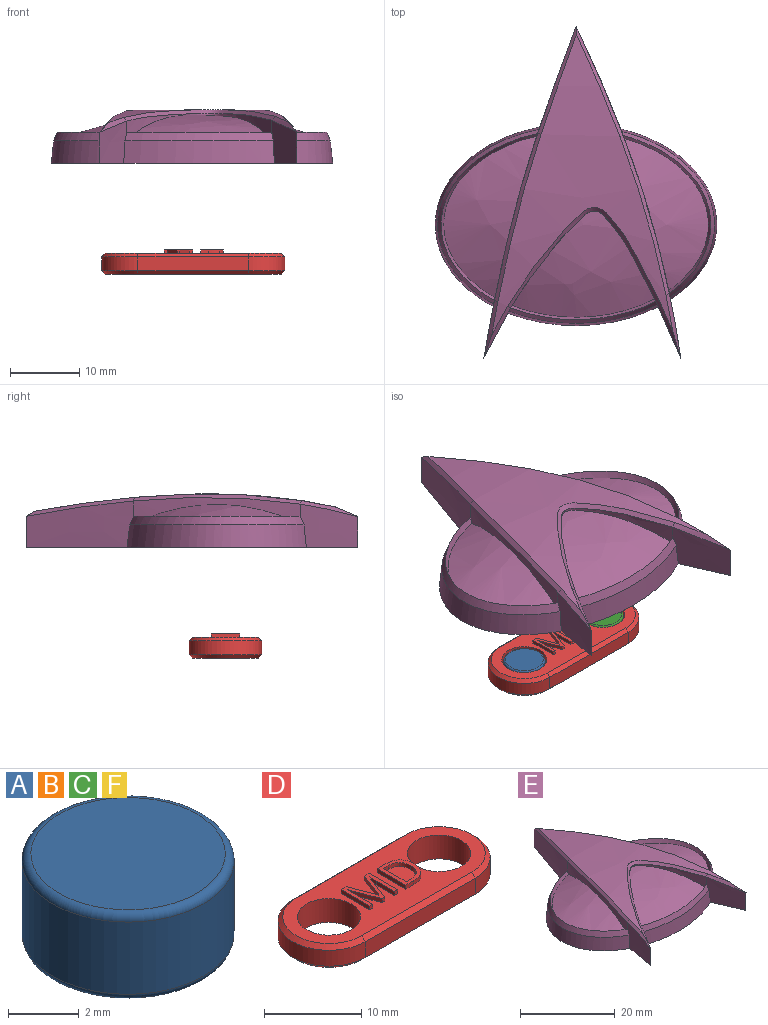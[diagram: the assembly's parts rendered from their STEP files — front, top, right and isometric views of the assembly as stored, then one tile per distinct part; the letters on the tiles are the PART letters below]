
ASSEMBLY  parts=6 mates=5
PART A: 5 faces, bbox 6.5x6.5x3 mm
  f0: cylinder r=3mm len=6mm, axis (0,0,-1), area 47.1mm2, adj f3,f4
  f1: plane 5.5x5.5mm, normal (0,0,1), area 23.8mm2, adj f4
  f2: plane 5.5x5.5mm, normal (0,0,-1), area 23.8mm2, adj f3
  f3: torus R=2.75mm, axis (0,0,1), area 7.2mm2, adj f0,f2
  f4: torus R=2.75mm, axis (0,0,1), area 7.2mm2, adj f0,f1
PART B: same geometry as A
PART C: same geometry as A
PART D: 51 faces, bbox 26.5x10.5x3.5 mm
  f0: plane 25.5x9.5mm, normal (0,0,1), area 137mm2, adj f4,f6,f8,f9,f10,f11,f16,f17
  f1: cylinder r=5.25mm len=10.5mm, axis (0,0,-1), area 33mm2, adj f2,f5,f9,f13
  f2: plane 16x2mm, normal (0,1,0), area 32mm2, adj f1,f3,f11,f15
  f3: cylinder r=5.25mm len=10.5mm, axis (0,0,-1), area 33mm2, adj f2,f5,f10,f14
  f4: cylinder r=3.25mm len=6.5mm, axis (0,0,-1), area 61.3mm2, adj f0,f7
  f5: plane 16x2mm, normal (0,-1,0), area 32mm2, adj f1,f3,f8,f12
  f6: cylinder r=3.25mm len=6.5mm, axis (0,0,-1), area 61.3mm2, adj f0,f7
  f7: plane 25.5x9.5mm, normal (0,0,-1), area 156.5mm2, adj f4,f6,f12,f13,f14,f15
  f8: plane 16x0.5mm, normal (0,-0.71,0.71), area 11.3mm2, adj f0,f5,f9,f10
  f9: cone r=5.25mm half-angle=45deg, axis (0,0,-1), area 11.1mm2, adj f0,f1,f8,f11
  f10: cone r=5.25mm half-angle=45deg, axis (0,0,-1), area 11.1mm2, adj f0,f3,f8,f11
  f11: plane 16x0.5mm, normal (0,0.71,0.71), area 11.3mm2, adj f0,f2,f9,f10
  f12: plane 16x0.5mm, normal (0,-0.71,-0.71), area 11.3mm2, adj f5,f7,f13,f14
  f13: cone r=4.75mm half-angle=45deg, axis (0,0,1), area 11.1mm2, adj f1,f7,f12,f15
  f14: cone r=4.75mm half-angle=45deg, axis (0,0,1), area 11.1mm2, adj f3,f7,f12,f15
  f15: plane 16x0.5mm, normal (0,0.71,-0.71), area 11.3mm2, adj f2,f7,f13,f14
  f16: plane 3.68x1.41mm, normal (-0.93,-0.36,0), area 2mm2, adj f0,f17,f33,f34
  f17: plane 0.5x0.39mm, normal (0,-1,0), area 0.2mm2, adj f0,f16,f18,f34
  f18: plane 3.67x1.42mm, normal (0.93,-0.36,0), area 2mm2, adj f0,f17,f19,f34
  f19: plane 0.5x0.02mm, normal (0,-1,0), area 0mm2, adj f0,f18,f20,f34
  f20: extruded ~1x0.5mm, area 0.5mm2, adj f0,f19,f21,f34
  f21: plane 2.67x0.5mm, normal (-1,0,0), area 1.3mm2, adj f0,f20,f22,f34
  f22: plane 0.5x0.48mm, normal (0,-1,0), area 0.2mm2, adj f0,f21,f23,f34
  f23: plane 4.15x0.5mm, normal (1,0,0), area 2.1mm2, adj f0,f22,f24,f34
  f24: plane 0.72x0.5mm, normal (0,1,0), area 0.4mm2, adj f0,f23,f25,f34
  f25: plane 3.42x1.32mm, normal (-0.93,0.36,0), area 1.8mm2, adj f0,f24,f26,f34
  f26: plane 0.5x0.02mm, normal (0,1,0), area 0mm2, adj f0,f25,f27,f34
  f27: plane 3.42x1.31mm, normal (0.93,0.36,0), area 1.8mm2, adj f0,f26,f28,f34
  f28: plane 0.73x0.5mm, normal (0,1,0), area 0.4mm2, adj f0,f27,f29,f34
  f29: plane 4.15x0.5mm, normal (-1,0,0), area 2.1mm2, adj f0,f28,f30,f34
  f30: plane 0.5x0.45mm, normal (0,-1,0), area 0.2mm2, adj f0,f29,f31,f34
  f31: plane 2.64x0.5mm, normal (1,0,0), area 1.3mm2, adj f0,f30,f32,f34
  f32: extruded ~1.04x0.5mm, area 0.5mm2, adj f0,f31,f33,f34
  f33: plane 0.5x0.02mm, normal (0,-1,0), area 0mm2, adj f0,f16,f32,f34
  f34: plane 4.15x4.11mm, normal (0,0,1), area 7.4mm2, adj f16,f17,f18,f19,f20,f21,f22,f23
  f35: extruded ~1.22x0.5mm, area 0.7mm2, adj f36,f48,f49,f50
  f36: extruded ~1.25x0.5mm, area 0.7mm2, adj f35,f37,f49,f50
  f37: extruded ~1.3x0.5mm, area 0.7mm2, adj f36,f38,f49,f50
  f38: plane 0.59x0.5mm, normal (0,1,0), area 0.3mm2, adj f37,f39,f49,f50
  f39: plane 3.31x0.5mm, normal (1,0,0), area 1.7mm2, adj f38,f40,f49,f50
  f40: plane 0.7x0.5mm, normal (0,-1,0), area 0.4mm2, adj f39,f48,f49,f50
  f41: extruded ~1.57x0.56mm, area 0.9mm2, adj f0,f42,f47,f49
  f42: extruded ~1.5x0.54mm, area 0.8mm2, adj f0,f41,f43,f49
  f43: extruded ~1.5x0.54mm, area 0.8mm2, adj f0,f42,f44,f49
  f44: plane 1.27x0.5mm, normal (0,1,0), area 0.6mm2, adj f0,f43,f45,f49
  f45: plane 4.15x0.5mm, normal (-1,0,0), area 2.1mm2, adj f0,f44,f46,f49
  f46: plane 1.15x0.5mm, normal (0,-1,0), area 0.6mm2, adj f0,f45,f47,f49
  f47: extruded ~1.6x0.54mm, area 0.9mm2, adj f0,f41,f46,f49
  f48: extruded ~1.21x0.5mm, area 0.7mm2, adj f35,f40,f49,f50
  f49: plane 4.15x3.31mm, normal (0,0,1), area 5.4mm2, adj f35,f36,f37,f38,f39,f40,f41,f42
  f50: plane 3.31x2.32mm, normal (0,0,1), area 6.7mm2, adj f35,f36,f37,f38,f39,f40,f48
PART E: 38 faces, bbox 40.7x49.4x10.5 mm
  f0: extruded ~15.84x6.82mm, area 96.5mm2, adj f1,f6,f11,f14,f19,f35
  f1: extruded ~15.54x6.73mm, area 92.1mm2, adj f0,f7,f13,f16,f19,f34
  f2: extruded ~8.33x6.27mm, area 42.7mm2, adj f3,f7,f13,f16,f19,f32
  f3: extruded ~7.25x6.13mm, area 41.8mm2, adj f2,f8,f12,f15,f19,f31,f32
  f4: extruded ~8.2x6.27mm, area 46.5mm2, adj f5,f8,f12,f15,f19,f29,f37
  f5: extruded ~9.35x6.42mm, area 49.3mm2, adj f4,f6,f11,f14,f19,f37
  f6: extruded ~22.81x6.67mm, area 45.6mm2, adj f0,f5,f9,f14,f17,f36
  f7: extruded ~24.13x6.24mm, area 41.9mm2, adj f1,f2,f16,f20,f21,f33
  f8: extruded ~20.99x13.98mm, area 33.8mm2, adj f3,f4,f10,f15,f18,f30
  f9: bspline ~22.81x12.77mm, area 30.4mm2, adj f6,f14,f17
  f10: bspline ~31.19x5.69mm, area 21.1mm2, adj f8,f15,f18
  f11: bspline ~24.68x13.97mm, area 110.5mm2, adj f0,f5,f14,f19
  f12: bspline ~32.34x5.76mm, area 72.8mm2, adj f3,f4,f15,f19
  f13: bspline ~28.83x22.98mm, area 121.1mm2, adj f1,f2,f16,f19
  f14: bspline ~23.95x13.54mm, area 43.8mm2, adj f0,f5,f6,f9,f11
  f15: bspline ~31.89x5.82mm, area 29.6mm2, adj f3,f4,f8,f10,f12
  f16: bspline ~28.17x22.62mm, area 48.2mm2, adj f1,f2,f7,f13,f20
  f17: bspline ~39x30.68mm, area 0mm2, adj f6,f9
  f18: bspline ~39x30.68mm, area 170.7mm2, adj f8,f10
  f19: plane 48x40.7mm, normal (0,0,-1), area 972mm2, adj f0,f1,f2,f3,f4,f5,f11,f12
  f20: bspline ~27.14x22.05mm, area 33.6mm2, adj f7,f16,f21
  f21: bspline ~39x30.68mm, area 0mm2, adj f7,f20
  f22: cylinder r=3.15mm len=6.3mm, axis (0,0,-1), area 59.4mm2, adj f19,f26
  f23: plane 2.3x2.3mm, normal (0,0,-1), area 4.2mm2, adj f26
  f24: cylinder r=3.15mm len=6.3mm, axis (0,0,-1), area 59.4mm2, adj f19,f27
  f25: plane 2.3x2.3mm, normal (0,0,-1), area 4.2mm2, adj f27
  f26: cone r=1.15mm half-angle=45deg, axis (0,0,-1), area 38.2mm2, adj f22,f23
  f27: cone r=1.15mm half-angle=45deg, axis (0,0,-1), area 38.2mm2, adj f24,f25
  f28: extruded ~43.47x26.21mm, area 343.4mm2, adj f29,f30,f31,f32,f33,f34,f35,f36
  f29: bspline ~8.75x4.27mm, area 5.1mm2, adj f4,f28,f30,f37
  f30: bspline ~21.95x14.56mm, area 27mm2, adj f8,f28,f29,f31
  f31: bspline ~7.81x4.54mm, area 4.8mm2, adj f3,f28,f30,f32
  f32: bspline ~8.97x2.43mm, area 5.2mm2, adj f2,f3,f28,f31,f33
  f33: bspline ~24.31x6.73mm, area 18.2mm2, adj f7,f28,f32,f34
  f34: bspline ~16.43x6.32mm, area 11.4mm2, adj f1,f28,f33,f35
  f35: bspline ~16.75x7.66mm, area 11.9mm2, adj f0,f28,f34,f36
  f36: bspline ~22.99x7.15mm, area 17.4mm2, adj f6,f28,f35,f37
  f37: bspline ~9.56x2.46mm, area 5.8mm2, adj f4,f5,f28,f29,f36
PART F: same geometry as A
PLACE A t=(-7.83,-0.1,-16)mm
PLACE B t=(8,0,0)mm
PLACE C t=(8.17,-0.1,-16)mm
PLACE D t=(0.17,-0.1,-16)mm
PLACE E at identity fixed
PLACE F t=(-8,0,0)mm
MATE fastened A.f0 <-> D.f4  axis (0,0,-1) through (-7.83,-0.1,-16)mm
MATE fastened C.f0 <-> D.f6  axis (0,0,-1) through (8.17,-0.1,-16)mm
MATE fastened E.f24 <-> F.f0  axis (0,0,-1) through (-8,0,0)mm
MATE slider E.f19 <-> D.f0  axis (0,0,-1) through (0.06,1.4,0)mm
MATE fastened E.f22 <-> B.f0  axis (0,0,-1) through (8,0,0)mm
